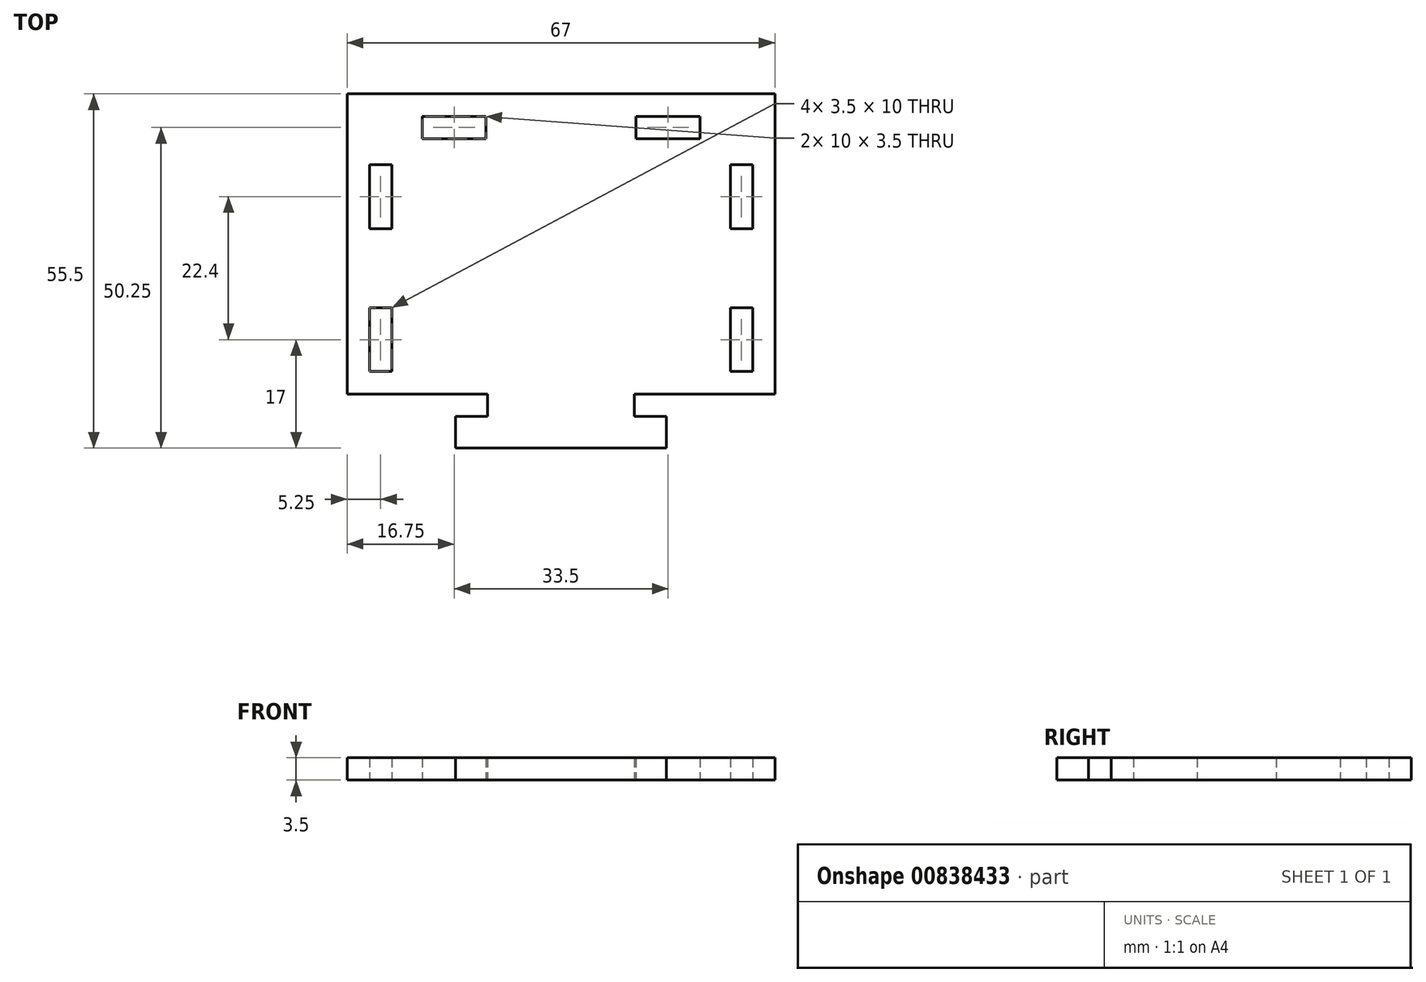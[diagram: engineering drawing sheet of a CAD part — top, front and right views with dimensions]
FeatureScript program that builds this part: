
annotation { "Feature Type Name" : "Feature", "Feature Type Description" : "" }
export const myFeature = defineFeature(function(context is Context, id is Id, definition is map)
    precondition{}
    {
        {
            var Q0;
            Q0=qCreatedBy(makeId("Top.planeOp"),FACE);
            var sketch = newSketch(context, id + "F0", { "sketchPlane" : qUnion([Q0])});
            skLineSegment(sketch, "E0", {"start": v(-33.5, 23.5) * mm, "end": v(0, 23.5) * mm});
            skLineSegment(sketch, "E1", {"start": v(33.5, 23.5) * mm, "end": v(33.5, -23.5) * mm});
            skLineSegment(sketch, "E2", {"start": v(33.5, -23.5) * mm, "end": v(11.5, -23.5) * mm});
            skLineSegment(sketch, "E3", {"start": v(11.5, -23.5) * mm, "end": v(11.5, -27) * mm});
            skLineSegment(sketch, "E4", {"start": v(11.5, -27) * mm, "end": v(16.5, -27) * mm});
            skLineSegment(sketch, "E5", {"start": v(16.5, -27) * mm, "end": v(16.5, -32) * mm});
            skLineSegment(sketch, "E6", {"start": v(16.5, -32) * mm, "end": v(-16.5, -32) * mm});
            skLineSegment(sketch, "E7", {"start": v(-16.5, -32) * mm, "end": v(-16.5, -27) * mm});
            skLineSegment(sketch, "E8", {"start": v(-16.5, -27) * mm, "end": v(-11.5, -27) * mm});
            skLineSegment(sketch, "E9", {"start": v(-11.5, -27) * mm, "end": v(-11.5, -23.5) * mm});
            skLineSegment(sketch, "E10", {"start": v(-11.5, -23.5) * mm, "end": v(-33.5, -23.5) * mm});
            skLineSegment(sketch, "E11", {"start": v(-33.5, -23.5) * mm, "end": v(-33.5, 23.5) * mm});
            skPoint(sketch, "E12", {"position": v(0, 23.5) * mm});
            skPoint(sketch, "E13", {"position": v(-33.5, 0) * mm});
            skLineSegment(sketch, "E14", {"start": v(0, 23.5) * mm, "end": v(33.5, 23.5) * mm});
            skPoint(sketch, "E15", {"position": v(-16.75, 23.5) * mm});
            skLineSegment(sketch, "E16.bottom", {"start": v(-11.75, 16.5) * mm, "end": v(-21.75, 16.5) * mm});
            skLineSegment(sketch, "E16.top", {"start": v(-11.75, 20) * mm, "end": v(-21.75, 20) * mm});
            skLineSegment(sketch, "E16.left", {"start": v(-11.75, 16.5) * mm, "end": v(-11.75, 20) * mm});
            skLineSegment(sketch, "E16.right", {"start": v(-21.75, 16.5) * mm, "end": v(-21.75, 20) * mm});
            skPoint(sketch, "E16.middle", {"position": v(-16.75, 18.25) * mm});
            skLineSegment(sketch, "E17.MirrorCS", {"start": v(21.75, 16.5) * mm, "end": v(21.75, 20) * mm});
            skLineSegment(sketch, "E18.MirrorCS", {"start": v(11.75, 20) * mm, "end": v(21.75, 20) * mm});
            skLineSegment(sketch, "E19.MirrorCS", {"start": v(11.75, 16.5) * mm, "end": v(11.75, 20) * mm});
            skLineSegment(sketch, "E20.MirrorCS", {"start": v(11.75, 16.5) * mm, "end": v(21.75, 16.5) * mm});
            skPoint(sketch, "E21.MirrorP", {"position": v(16.75, 18.25) * mm});
            skLineSegment(sketch, "E22.bottom", {"start": v(-26.5, 12.4) * mm, "end": v(-30, 12.4) * mm});
            skLineSegment(sketch, "E22.top", {"start": v(-26.5, 2.4) * mm, "end": v(-30, 2.4) * mm});
            skLineSegment(sketch, "E22.left", {"start": v(-26.5, 12.4) * mm, "end": v(-26.5, 2.4) * mm});
            skLineSegment(sketch, "E22.right", {"start": v(-30, 12.4) * mm, "end": v(-30, 2.4) * mm});
            skPoint(sketch, "E22.middle", {"position": v(-28.25, 7.4) * mm});
            skLineSegment(sketch, "E23.MirrorCS", {"start": v(30, 12.4) * mm, "end": v(30, 2.4) * mm});
            skLineSegment(sketch, "E24.MirrorCS", {"start": v(26.5, 12.4) * mm, "end": v(26.5, 2.4) * mm});
            skLineSegment(sketch, "E25.MirrorCS", {"start": v(26.5, 2.4) * mm, "end": v(30, 2.4) * mm});
            skLineSegment(sketch, "E26.MirrorCS", {"start": v(26.5, 12.4) * mm, "end": v(30, 12.4) * mm});
            skPoint(sketch, "E27.MirrorP", {"position": v(28.25, 7.4) * mm});
            skLineSegment(sketch, "E28.0.1.0", {"start": v(-26.5, -10) * mm, "end": v(-30, -10) * mm});
            skLineSegment(sketch, "E28.0.1.1", {"start": v(-26.5, -20) * mm, "end": v(-30, -20) * mm});
            skPoint(sketch, "E28.0.1.2", {"position": v(-28.25, -15) * mm});
            skLineSegment(sketch, "E28.0.1.3", {"start": v(-26.5, -10) * mm, "end": v(-26.5, -20) * mm});
            skLineSegment(sketch, "E28.0.1.4", {"start": v(-30, -10) * mm, "end": v(-30, -20) * mm});
            skLineSegment(sketch, "E28.0.1.5", {"start": v(26.5, -20) * mm, "end": v(30, -20) * mm});
            skPoint(sketch, "E28.0.1.6", {"position": v(28.25, -15) * mm});
            skLineSegment(sketch, "E28.0.1.7", {"start": v(30, -10) * mm, "end": v(30, -20) * mm});
            skLineSegment(sketch, "E28.0.1.8", {"start": v(26.5, -10) * mm, "end": v(26.5, -20) * mm});
            skLineSegment(sketch, "E28.0.1.9", {"start": v(26.5, -10) * mm, "end": v(30, -10) * mm});
            skLineSegment(sketch, "E28.direction1", {"start": v(-30, 2.4) * mm, "end": v(5.8, 2.4) * mm, "construction": true});
            skLineSegment(sketch, "E28.direction2", {"start": v(-30, 2.4) * mm, "end": v(-30, -20) * mm, "construction": true});
            skSolve(sketch);
        }
        {
            var Q0;
            Q0=makeQuery(id+"F0.imprint","IMPRINT",FACE,{"disambiguationData":[TD([[makeQuery(id+"F0.imprint","IMPRINT",EDGE,{"derivedFrom":sQuery(id+"F0.wireOp",EDGE,"E0")}),-1.0]])]});
            extrude(context, id + "F1", {"entities" : qUnion([Q0]), "depth" : 3.5 * mm, "offsetDistance" : 25 * mm});
        }
    });
